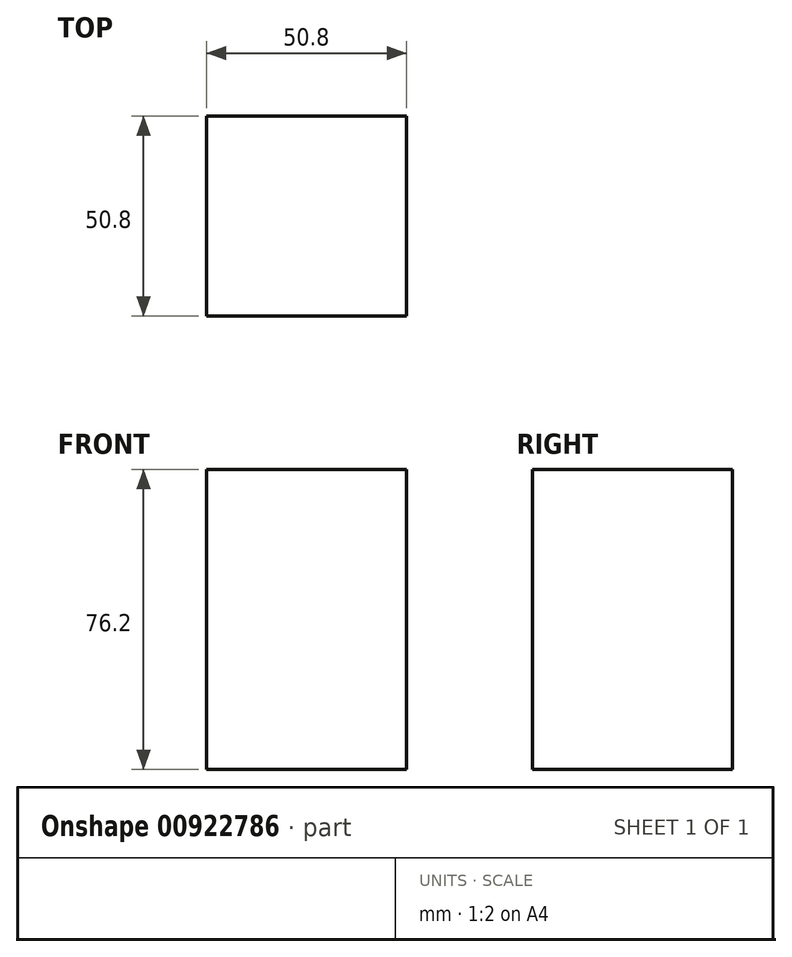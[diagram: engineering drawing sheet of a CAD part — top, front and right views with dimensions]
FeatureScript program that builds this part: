
annotation { "Feature Type Name" : "Feature", "Feature Type Description" : "" }
export const myFeature = defineFeature(function(context is Context, id is Id, definition is map)
    precondition{}
    {
        {
            var Q0;
            Q0=qCreatedBy(makeId("Top.planeOp"),FACE);
            var sketch = newSketch(context, id + "F0", { "sketchPlane" : qUnion([Q0])});
            skLineSegment(sketch, "E0.bottom", {"start": v(-24.27, 16.84) * mm, "end": v(26.53, 16.84) * mm});
            skLineSegment(sketch, "E0.top", {"start": v(-24.27, -33.96) * mm, "end": v(26.53, -33.96) * mm});
            skLineSegment(sketch, "E0.left", {"start": v(-24.27, 16.84) * mm, "end": v(-24.27, -33.96) * mm});
            skLineSegment(sketch, "E0.right", {"start": v(26.53, 16.84) * mm, "end": v(26.53, -33.96) * mm});
            skSolve(sketch);
        }
        {
            var Q0;
            Q0 = qSketchRegion(id + "F0", true);
            extrude(context, id + "F1", {"entities" : qUnion([Q0]), "depth" : 76.2 * mm, "offsetDistance" : 25.4 * mm});
        }
    });
